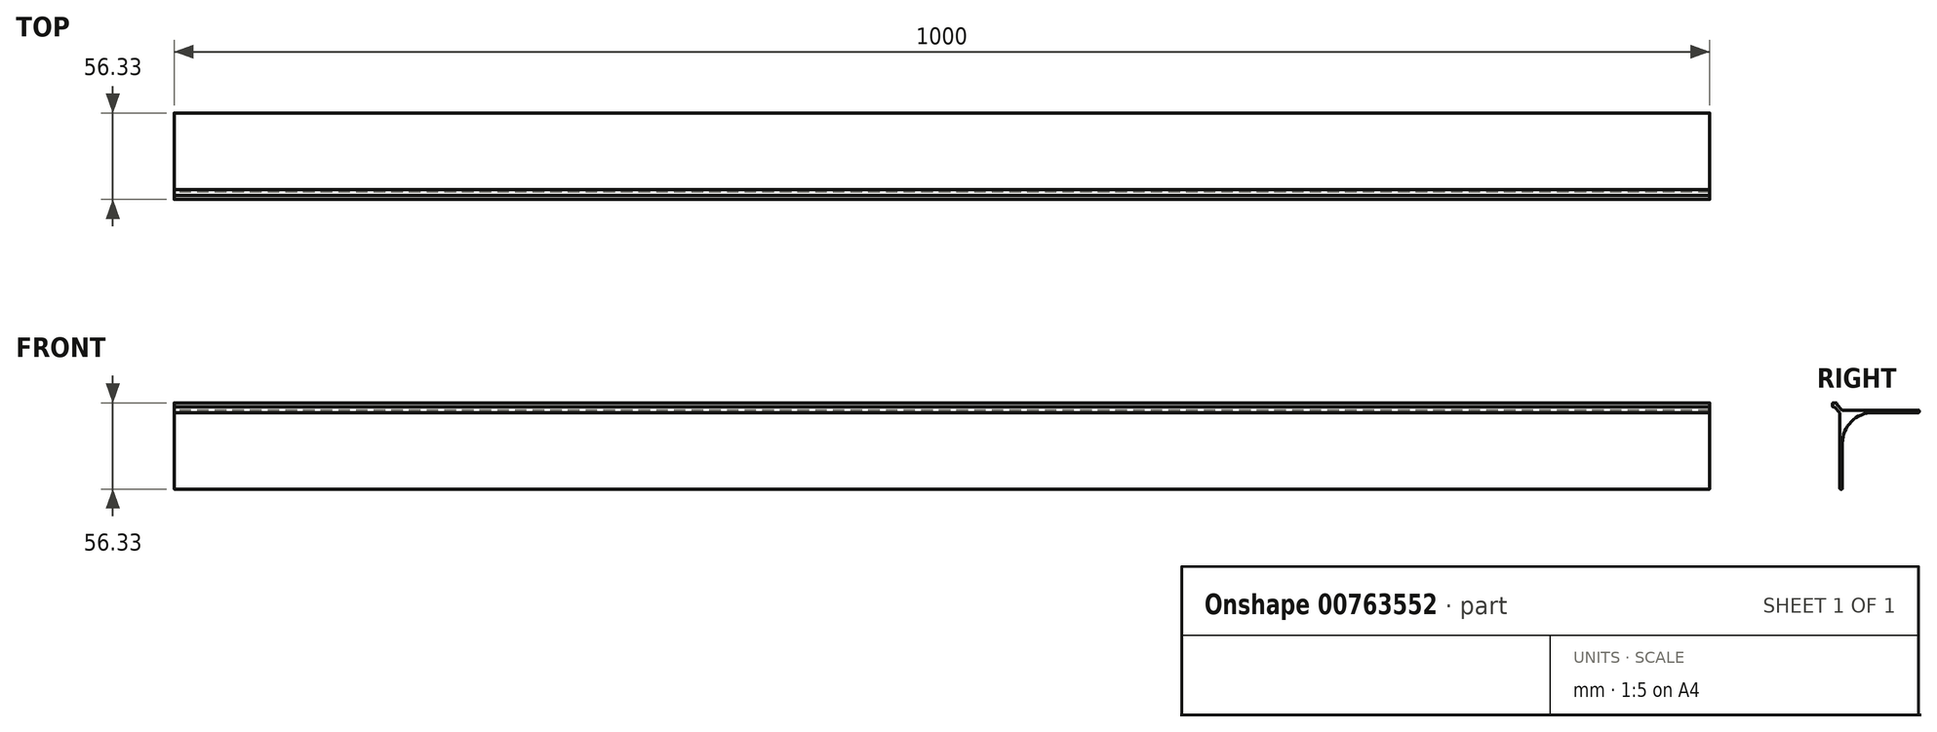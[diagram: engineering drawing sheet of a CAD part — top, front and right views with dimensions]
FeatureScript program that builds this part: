
annotation { "Feature Type Name" : "Feature", "Feature Type Description" : "" }
export const myFeature = defineFeature(function(context is Context, id is Id, definition is map)
    precondition{}
    {
        {
            var Q0;
            Q0=qCreatedBy(makeId("Right.planeOp"),FACE);
            var sketch = newSketch(context, id + "F0", { "sketchPlane" : qUnion([Q0])});
            skLineSegment(sketch, "E0", {"start": v(0, 0.5) * mm, "end": v(0, 50) * mm});
            skLineSegment(sketch, "E1", {"start": v(1.56, 51.56) * mm, "end": v(51.06, 51.56) * mm});
            skLineSegment(sketch, "E2", {"start": v(51.56, 51.06) * mm, "end": v(51.56, 50.46) * mm});
            skLineSegment(sketch, "E3", {"start": v(51.06, 49.96) * mm, "end": v(21.6, 49.96) * mm});
            skLineSegment(sketch, "E4", {"start": v(1.6, 29.96) * mm, "end": v(1.6, 0.5) * mm});
            skLineSegment(sketch, "E5", {"start": v(1.1, 0) * mm, "end": v(0.5, 0) * mm});
            skLineSegment(sketch, "E6", {"start": v(1.56, 51.56) * mm, "end": v(-2.05, 55.16) * mm});
            skLineSegment(sketch, "E7", {"start": v(-2.12, 55.23) * mm, "end": v(-2.12, 55.23) * mm});
            skLineSegment(sketch, "E8", {"start": v(0, 50) * mm, "end": v(-3.6, 53.6) * mm});
            skLineSegment(sketch, "E9", {"start": v(-3.78, 53.68) * mm, "end": v(-4.47, 53.68) * mm});
            skLineSegment(sketch, "E10", {"start": v(-4.77, 53.98) * mm, "end": v(-4.77, 56.03) * mm});
            skLineSegment(sketch, "E11", {"start": v(-2.42, 56.33) * mm, "end": v(-4.47, 56.33) * mm});
            skLineSegment(sketch, "E12", {"start": v(-2.12, 55.34) * mm, "end": v(-2.12, 56.03) * mm});
            skPoint(sketch, "E13.visualSharp", {"position": v(-2.12, 56.33) * mm});
            skArc(sketch, "E13.filletArc", {"start": v(-2.12, 56.03) * mm, "mid": v(-2.2, 56.24) * mm, "end": v(-2.42, 56.33) * mm});
            skPoint(sketch, "E14.visualSharp", {"position": v(-4.77, 53.68) * mm});
            skArc(sketch, "E14.filletArc", {"start": v(-4.77, 53.98) * mm, "mid": v(-4.69, 53.76) * mm, "end": v(-4.47, 53.68) * mm});
            skPoint(sketch, "E15.visualSharp", {"position": v(-4.77, 56.33) * mm});
            skArc(sketch, "E15.filletArc", {"start": v(-4.47, 56.33) * mm, "mid": v(-4.69, 56.24) * mm, "end": v(-4.77, 56.03) * mm});
            skPoint(sketch, "E16.visualSharp", {"position": v(1.6, 49.96) * mm});
            skPoint(sketch, "E17.visualSharp", {"position": v(-3.68, 53.68) * mm});
            skArc(sketch, "E17.filletArc", {"start": v(-3.6, 53.6) * mm, "mid": v(-3.68, 53.66) * mm, "end": v(-3.78, 53.68) * mm});
            skPoint(sketch, "E18.visualSharp", {"position": v(-2.12, 55.23) * mm});
            skArc(sketch, "E18.filletArc", {"start": v(-2.12, 55.34) * mm, "mid": v(-2.1, 55.24) * mm, "end": v(-2.05, 55.16) * mm});
            skArc(sketch, "E19.filletArc", {"start": v(21.6, 49.96) * mm, "mid": v(7.46, 44.1) * mm, "end": v(1.6, 29.96) * mm});
            skPoint(sketch, "E20.visualSharp", {"position": v(51.56, 49.96) * mm});
            skArc(sketch, "E20.filletArc", {"start": v(51.06, 49.96) * mm, "mid": v(51.4, 50.1) * mm, "end": v(51.56, 50.46) * mm});
            skPoint(sketch, "E21.visualSharp", {"position": v(51.56, 51.56) * mm});
            skArc(sketch, "E21.filletArc", {"start": v(51.56, 51.06) * mm, "mid": v(51.4, 51.4) * mm, "end": v(51.06, 51.56) * mm});
            skPoint(sketch, "E22.visualSharp", {"position": v(1.6, 0) * mm});
            skArc(sketch, "E22.filletArc", {"start": v(1.1, 0) * mm, "mid": v(1.45, 0.15) * mm, "end": v(1.6, 0.5) * mm});
            skPoint(sketch, "E23.visualSharp", {"position": v(0, 0) * mm});
            skArc(sketch, "E23.filletArc", {"start": v(0, 0.5) * mm, "mid": v(0.15, 0.15) * mm, "end": v(0.5, 0) * mm});
            skSolve(sketch);
        }
        {
            var Q0;
            Q0=makeQuery(id+"F0.imprint","IMPRINT",FACE,{"disambiguationData":[TD([[makeQuery(id+"F0.imprint","IMPRINT",EDGE,{"derivedFrom":sQuery(id+"F0.wireOp",EDGE,"E0")}),-1.0]])]});
            extrude(context, id + "F1", {"entities" : qUnion([Q0]), "depth" : 1000 * mm, "offsetDistance" : 25 * mm});
        }
    });
